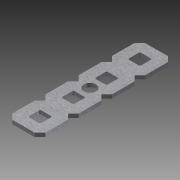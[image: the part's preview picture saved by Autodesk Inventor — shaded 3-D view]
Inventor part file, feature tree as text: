
AUTODESK INVENTOR PART (.ipt)
format: ipt  version: 2012 (Build 160160000, 160)  size: 749,056 bytes
history: native  units: in
note: dims shown in document units (in); Inventor stores cm internally (conversion verified against a paired STEP export)
features: other x4, sketch x2, imported_body x1, plane x1, split x1, hole x1
ambient origin geometry x8: Origin, YZ Plane, XZ Plane, XY Plane, X Axis, Y Axis, Z Axis, Center Point
feature tree (10):
  parser-record x1  (decoder bookkeeping rows leaked as tree rows — omitted from the tree; the rows remain in map.json)
  imported_body  "Base1"
  sketch  "Sketch1"  dims[d0=9.8425in d2=0.5in d3=0.3937in d5=1.0in d7=0.182in]
  plane  "Work Plane1"
  split  "Split1"
  other  "Work Point1"
  hole  "Hole1"  [1 undecoded]
  other  "Work Axis1"
  other  "Work Axis2"
  sketch  "Sketch2"  dims[d8=0.182in d9=0.75in d10=0.375in d11=0.25in d12=0.5635in d13=1.0in d14=0.8108in]
note: 1 required parameter value undecoded (feature->parameter linkage not recoverable at this tier; creation-order binding heuristic only, values carry confidence <= 0.55)
